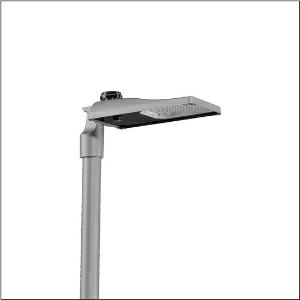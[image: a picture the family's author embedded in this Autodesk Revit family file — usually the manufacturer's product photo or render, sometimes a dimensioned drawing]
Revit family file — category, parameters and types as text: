
# Revit family: streetlight_sl_31_mini___st1_0a_5xh6d3bm08ga_d2dc
name_source: partatom
category: Lighting Fixtures
units: mm (PartAtom-declared; Revit-internal decimal feet)

## family parameters
Cut with Voids When Loaded = No
Host = Face
Light Source = No
Part Type = Normal
Room Calculation Point = No
Round Connector Dimension = Use Diameter
Shared = No

## types (1)
- --- (1 x LED, 5880 lm, 39.3 W, 3000K)
    Apparent Load = 39 VA
    CIE Flux Codes = 37 72 97 100 100
    Color Rendering = 70
    Color Temperature = 3000K
    Default Elevation = 1800 mm
    Description = Streetlight SL 31 mini, mast luminaire, primary light control with lens, of PMMA, primary optical cover: cover, of toughened safety glass, transparent, light distribution: ST1.0a, light emission: direct distribution, primary light characteristic: asymmetric, installation type: post-top, side-entry, LED, High Power LED, rated luminous flux: 5.880lm, luminous efficacy: 150lm/W, light colour: 730, colour temperature: 3000K, control: presetting dimming linear, flexible luminous flux parameterisation, time-dependent luminous flux control, constant luminous flux control, intelligent temperature release in ECG and LED module, overheat protection, with cable H07RN-F 3x 1.5mm², mains connection: 220..240V, AC, 50/60Hz, connection cable pre-assembled, cable length: 6,5m, start of lifetime: 39W, end of service life: 41W, reduction: 18W, luminaire housing, of diecast aluminium, powder-coated, Siteco® metallic grey (DB 702S), corrosivity category C5 high according to DIN EN ISO 12944, no sealing on luminaire upper side, inclination: -15°..+20° (post-top) | -20°..+20° (side-entry), adjustable in 5° steps, mast flange (76/60mm) included as standard, multi-level sealing system, sealing non-destructively replaceable, Smart Interface below, protection rating (complete): IP66, insulation class (complete): insulation class I (protective earthing), certification: CE, ENEC, ENEC+, VDE, UKCA, impact resistance: IK09, permissible operating ambient temperature for outdoor applications: -40..+50°C, standard-compliant lighting for roads and squares, packaging unit: 1 piece

Light Distribution: ST1.0a
    Height = 76 mm
    Lamp = 1 x LED
    Lamp Light Flux = 5880 lm
    Lamp Power = 39.3 W
    Lamp count = 1
    Length = 547 mm
    Luminous efficacy = 150 lm/W
    Manufacturer = Siteco
    ModVariant = No
    Model = 5XH6D3BM08GA
    Number of Poles = 1
    OnlyDefault = Yes
    Power Factor = 1
    Product Name = Streetlight SL 31 mini | ST1.0a
    Product group = mast luminaire | pylon top
    ProductGroupID = 6100
    Protection Class = Protection class I
    Protection Degree = IP 66
    RLX_Detail_Level = 1
    RLX_Emergency_Light_Flux = 0 lm
    RLX_Emergency_Type = 0
    RLX_Emergency_Type_DB = No
    RlxData = <blob elided: 40637 chars, md5=c7aa4e20>
    Socket = socket
    Standby Power = 0 W
    System Light Flux = 5880 lm
    System Power = 39 W
    Type Comments = factory setting: luminous flux: 100 % | dim-lin: 254 | 798 mA
    Type Image = l_1300324.jpg
    URL = http://relux.com
    VarID = @adj_011363
    Voltage = 0 V
    Weight = 0.00 kg
    Width = 265 mm

## geometry (parser evidence)
native form markers: Blend x4, Sweep x9
no freeform markers — native parametric forms only
